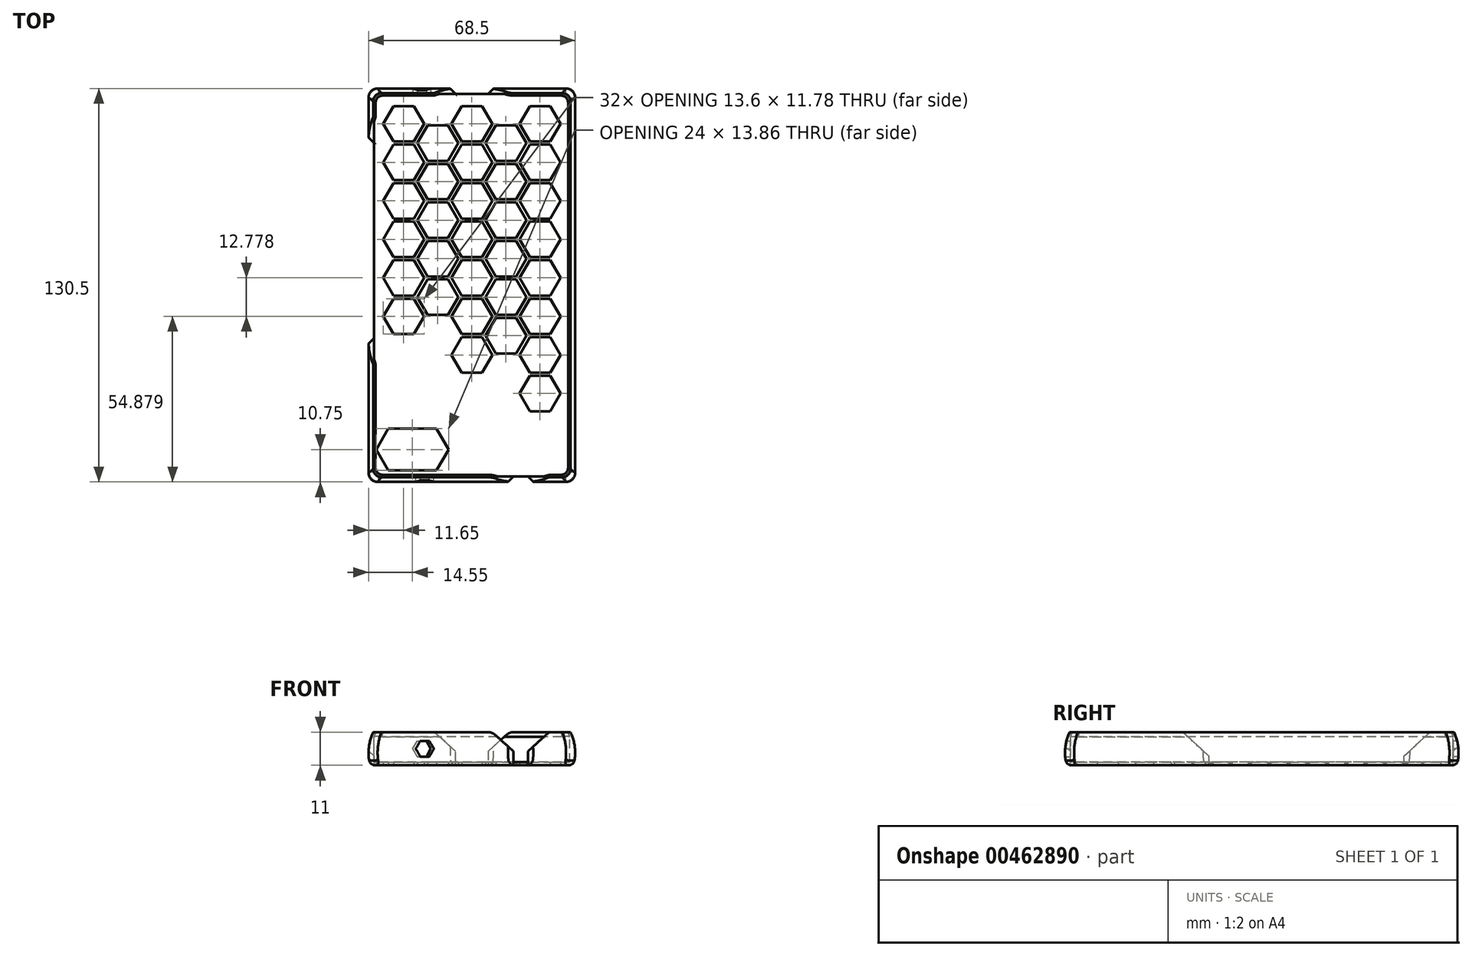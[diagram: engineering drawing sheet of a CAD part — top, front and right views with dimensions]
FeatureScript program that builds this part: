
annotation { "Feature Type Name" : "Feature", "Feature Type Description" : "" }
export const myFeature = defineFeature(function(context is Context, id is Id, definition is map)
    precondition{}
    {
        {
            var Q0;
            Q0=qCreatedBy(makeId("Top.planeOp"),FACE);
            var sketch = newSketch(context, id + "F0", { "sketchPlane" : qUnion([Q0])});
            skLineSegment(sketch, "E0.bottom", {"start": v(-32.9, 63.9) * mm, "end": v(32.9, 63.9) * mm});
            skLineSegment(sketch, "E0.top", {"start": v(-32.9, -63.9) * mm, "end": v(32.9, -63.9) * mm});
            skLineSegment(sketch, "E0.left", {"start": v(-32.9, 63.9) * mm, "end": v(-32.9, -63.9) * mm});
            skLineSegment(sketch, "E0.right", {"start": v(32.9, 63.9) * mm, "end": v(32.9, -63.9) * mm});
            skLineSegment(sketch, "E1", {"start": v(-32.9, 63.9) * mm, "end": v(32.9, -63.9) * mm, "construction": true});
            skLineSegment(sketch, "E2.bottom", {"start": v(-34.1, 65.1) * mm, "end": v(34.1, 65.1) * mm});
            skLineSegment(sketch, "E2.top", {"start": v(-34.1, -65.1) * mm, "end": v(34.1, -65.1) * mm});
            skLineSegment(sketch, "E2.left", {"start": v(-34.1, 65.1) * mm, "end": v(-34.1, -65.1) * mm});
            skLineSegment(sketch, "E2.right", {"start": v(34.1, 65.1) * mm, "end": v(34.1, -65.1) * mm});
            skLineSegment(sketch, "E3", {"start": v(34.1, 65.1) * mm, "end": v(-34.1, -65.1) * mm, "construction": true});
            skSolve(sketch);
        }
        {
            var Q0;
            Q0=makeQuery(id+"F0.imprint","IMPRINT",FACE,{"disambiguationData":[TD([[makeQuery(id+"F0.imprint","IMPRINT",EDGE,{"derivedFrom":sQuery(id+"F0.wireOp",EDGE,"E0.bottom")}),-1.0]])]});
            extrude(context, id + "F1", {"entities" : qUnion([Q0]), "depth" : 1 * mm});
        }
        {
            var Q0;
            Q0=makeQuery(id+"F1.opExtrude","SWEPT_FACE",FACE,{"disambiguationData":[OSD([sQuery(id+"F0.wireOp",EDGE,"E0.right")])]});
            var sketch = newSketch(context, id + "F2", { "sketchPlane" : qUnion([Q0])});
            skLineSegment(sketch, "E4", {"start": v(-63.9, 0) * mm, "end": v(-64.7, 0) * mm});
            skPoint(sketch, "E5.startSnap0", {"position": v(-64.3, 0) * mm});
            skLineSegment(sketch, "E6", {"start": v(-62.9, 11) * mm, "end": v(-63.7, 11) * mm});
            skArc(sketch, "E7", {"start": v(-63.7, 11) * mm, "mid": v(-65.18, 5.59) * mm, "end": v(-64.7, 0) * mm});
            skLineSegment(sketch, "E8", {"start": v(-63.9, 0) * mm, "end": v(-63.9, 1) * mm});
            skArc(sketch, "E9", {"start": v(-62.9, 11) * mm, "mid": v(-64.06, 6.07) * mm, "end": v(-63.9, 1) * mm});
            skLineSegment(sketch, "E10", {"start": v(-49.25, 4.14) * mm, "end": v(-44.8, 4.14) * mm, "construction": true});
            skLineSegment(sketch, "E11", {"start": v(-62.9, 11) * mm, "end": v(-62.9, 1) * mm, "construction": true});
            skLineSegment(sketch, "E12", {"start": v(-63.43, 1) * mm, "end": v(-63.43, 9.4) * mm});
            skSolve(sketch);
        }
        {
            var Q0;
            Q0=makeQuery(id+"F2.imprint","IMPRINT",FACE,{"disambiguationData":[TD([[makeQuery(id+"F2.imprint","IMPRINT",EDGE,{"derivedFrom":sQuery(id+"F2.wireOp",EDGE,"E4")}),-1.0]])]});
            var Q1;
            {var subQ3=sQuery(id+"F2.wireOp",EDGE,"E12");Q1=makeQuery(id+"F2.imprint","IMPRINT",FACE,{"disambiguationData":[TD([[makeQuery(id+"F2.imprint","IMPRINT",EDGE,{"derivedFrom":subQ3}),1.0]])]});}
            var Q2;
            Q2=makeQuery(id+"F1.opExtrude","CAP_EDGE",EDGE,{"disambiguationData":[OSD([sQuery(id+"F0.wireOp",EDGE,"E0.top")])],"isStart":false});
            var Q3;
            Q3=makeQuery(id+"F1.opExtrude","CAP_EDGE",EDGE,{"disambiguationData":[OSD([sQuery(id+"F0.wireOp",EDGE,"E0.left")])],"isStart":false});
            var Q4;
            Q4=makeQuery(id+"F1.opExtrude","CAP_EDGE",EDGE,{"disambiguationData":[OSD([sQuery(id+"F0.wireOp",EDGE,"E0.bottom")])],"isStart":false});
            var Q5;
            Q5=makeQuery(id+"F1.opExtrude","CAP_EDGE",EDGE,{"disambiguationData":[OSD([sQuery(id+"F0.wireOp",EDGE,"E0.right")])],"isStart":false});
            sweep(context, id + "F3", {"operationType" : NewBodyOperationType.ADD, "profiles" : qUnion([Q0, Q1]), "path" : qUnion([Q2, Q3, Q4, Q5])});
        }
        {
            var Q0;
            Q0=makeQuery(id+"F3.opSweep","MID_CAP_EDGE",EDGE,{"disambiguationData":[OSD([sQuery(id+"F0.wireOp",EDGE,"E0.bottom"),sQuery(id+"F0.wireOp",EDGE,"E0.right"),sQuery(id+"F2.wireOp",EDGE,"E7")])],"capPos":3.0});
            var Q1;
            Q1=makeQuery(id+"F3.opSweep","MID_CAP_EDGE",EDGE,{"disambiguationData":[OSD([sQuery(id+"F0.wireOp",EDGE,"E0.bottom"),sQuery(id+"F0.wireOp",EDGE,"E0.left"),sQuery(id+"F2.wireOp",EDGE,"E7")])],"capPos":2.0});
            var Q2;
            Q2=makeQuery(id+"F3.opSweep","MID_CAP_EDGE",EDGE,{"disambiguationData":[OSD([sQuery(id+"F0.wireOp",EDGE,"E0.top"),sQuery(id+"F0.wireOp",EDGE,"E0.left"),sQuery(id+"F2.wireOp",EDGE,"E7")])],"capPos":1.0});
            var Q3;
            Q3=makeQuery(id+"F3.opSweep","CAP_EDGE",EDGE,{"disambiguationData":[OSD([sQuery(id+"F0.wireOp",EDGE,"E0.top"),sQuery(id+"F0.wireOp",EDGE,"E0.right"),sQuery(id+"F2.wireOp",EDGE,"E7")])],"isStart":true});
            fillet(context, id + "F4", {"entities" : qUnion([Q0, Q1, Q2, Q3]), "radius" : 3 * mm, "tangentPropagation" : true, "allowEdgeOverflow" : false});
        }
        {
            var Q0;
            Q0=makeQuery(id+"F3.opSweep","MID_CAP_EDGE",EDGE,{"disambiguationData":[OSD([sQuery(id+"F0.wireOp",EDGE,"E0.bottom"),sQuery(id+"F0.wireOp",EDGE,"E0.right"),sQuery(id+"F2.wireOp",EDGE,"0y0pLbtj-wvh3-Di3X-naMg-oC3GUoqOavBz")])],"capPos":3.0});
            var Q1;
            Q1=makeQuery(id+"F3.opSweep","MID_CAP_EDGE",EDGE,{"disambiguationData":[OSD([sQuery(id+"F0.wireOp",EDGE,"E0.bottom"),sQuery(id+"F0.wireOp",EDGE,"E0.left"),sQuery(id+"F2.wireOp",EDGE,"0y0pLbtj-wvh3-Di3X-naMg-oC3GUoqOavBz")])],"capPos":2.0});
            var Q2;
            Q2=makeQuery(id+"F3.opSweep","CAP_EDGE",EDGE,{"disambiguationData":[OSD([sQuery(id+"F0.wireOp",EDGE,"E0.top"),sQuery(id+"F0.wireOp",EDGE,"E0.right"),sQuery(id+"F2.wireOp",EDGE,"0y0pLbtj-wvh3-Di3X-naMg-oC3GUoqOavBz")])],"isStart":true});
            var Q3;
            Q3=makeQuery(id+"F3.opSweep","MID_CAP_EDGE",EDGE,{"disambiguationData":[OSD([sQuery(id+"F0.wireOp",EDGE,"E0.top"),sQuery(id+"F0.wireOp",EDGE,"E0.left"),sQuery(id+"F2.wireOp",EDGE,"0y0pLbtj-wvh3-Di3X-naMg-oC3GUoqOavBz")])],"capPos":1.0});
            fillet(context, id + "F5", {"entities" : qUnion([Q0, Q1, Q2, Q3]), "radius" : 2.6 * mm, "tangentPropagation" : true, "allowEdgeOverflow" : false});
        }
        {
            var Q0;
            {var subQ0=sQuery(id+"F0.wireOp",EDGE,"E0.top");Q0=makeQuery(id+"F3.boolean.opBoolean","MERGE",FACE,{"derivedFrom":[makeQuery(id+"F1.opExtrude","CAP_FACE",FACE,{"disambiguationData":[OSD([sQuery(id+"F0.wireOp",EDGE,"E0.bottom"),subQ0,sQuery(id+"F0.wireOp",EDGE,"E0.left"),sQuery(id+"F0.wireOp",EDGE,"E0.right")])],"isStart":true}),makeQuery(id+"F3.opSweep","SWEPT_FACE",FACE,{"disambiguationData":[OSD([subQ0,sQuery(id+"F2.wireOp",EDGE,"E4")])]})]});}
            var sketch = newSketch(context, id + "F6", { "sketchPlane" : qUnion([Q0])});
            skLineSegment(sketch, "E13", {"start": v(0, -64.7) * mm, "end": v(0, 64.7) * mm, "construction": true});
            skLineSegment(sketch, "E14", {"start": v(-26, -34.85) * mm, "end": v(-29.4, -40.74) * mm});
            skLineSegment(sketch, "E15", {"start": v(-29.4, -40.74) * mm, "end": v(-26, -46.63) * mm});
            skLineSegment(sketch, "E16", {"start": v(-26, -46.63) * mm, "end": v(-19.2, -46.63) * mm});
            skLineSegment(sketch, "E17", {"start": v(-19.2, -46.63) * mm, "end": v(-15.8, -40.74) * mm});
            skLineSegment(sketch, "E18", {"start": v(-15.8, -40.74) * mm, "end": v(-19.2, -34.85) * mm});
            skLineSegment(sketch, "E19", {"start": v(-19.2, -34.85) * mm, "end": v(-26, -34.85) * mm});
            skLineSegment(sketch, "E20", {"start": v(-26, -34.85) * mm, "end": v(-26, -46.63) * mm, "construction": true});
            skLineSegment(sketch, "E21", {"start": v(-33.7, -40.74) * mm, "end": v(-29.4, -40.74) * mm, "construction": true});
            skLineSegment(sketch, "E22", {"start": v(-26, -46.63) * mm, "end": v(-19.2, -34.85) * mm, "construction": true});
            skLineSegment(sketch, "E23", {"start": v(-29.4, -40.74) * mm, "end": v(-15.8, -40.74) * mm, "construction": true});
            skLineSegment(sketch, "E24", {"start": v(-11.3, -64.7) * mm, "end": v(-11.3, 64.7) * mm, "construction": true});
            skLineSegment(sketch, "E25", {"start": v(-15.8, -40.74) * mm, "end": v(-11.3, -40.74) * mm, "construction": true});
            skLineSegment(sketch, "E26", {"start": v(-26, -34.85) * mm, "end": v(-19.2, -46.63) * mm, "construction": true});
            skLineSegment(sketch, "E27.MirrorCS", {"start": v(-6.8, -40.74) * mm, "end": v(-3.4, -34.85) * mm});
            skLineSegment(sketch, "E28.MirrorCS", {"start": v(-3.4, -34.85) * mm, "end": v(3.4, -34.85) * mm});
            skLineSegment(sketch, "E29.MirrorCS", {"start": v(3.4, -34.85) * mm, "end": v(6.8, -40.74) * mm});
            skLineSegment(sketch, "E30.MirrorCS", {"start": v(6.8, -40.74) * mm, "end": v(3.4, -46.63) * mm});
            skLineSegment(sketch, "E31.MirrorCS", {"start": v(3.4, -46.63) * mm, "end": v(-3.4, -46.63) * mm});
            skLineSegment(sketch, "E32.MirrorCS", {"start": v(-3.4, -46.63) * mm, "end": v(-6.8, -40.74) * mm});
            skPoint(sketch, "E33", {"position": v(0, -34.85) * mm});
            skLineSegment(sketch, "E34", {"start": v(11.3, -64.7) * mm, "end": v(11.3, 64.7) * mm, "construction": true});
            skLineSegment(sketch, "E35", {"start": v(6.8, -40.74) * mm, "end": v(11.3, -40.74) * mm, "construction": true});
            skLineSegment(sketch, "E36.MirrorCS", {"start": v(19.2, -34.85) * mm, "end": v(15.8, -40.74) * mm});
            skLineSegment(sketch, "E37.MirrorCS", {"start": v(26, -34.85) * mm, "end": v(19.2, -34.85) * mm});
            skLineSegment(sketch, "E38.MirrorCS", {"start": v(29.4, -40.74) * mm, "end": v(26, -34.85) * mm});
            skLineSegment(sketch, "E39.MirrorCS", {"start": v(26, -46.63) * mm, "end": v(29.4, -40.74) * mm});
            skLineSegment(sketch, "E40.MirrorCS", {"start": v(19.2, -46.63) * mm, "end": v(26, -46.63) * mm});
            skLineSegment(sketch, "E41.MirrorCS", {"start": v(15.8, -40.74) * mm, "end": v(19.2, -46.63) * mm});
            skLineSegment(sketch, "E42", {"start": v(-4.5, -34.35) * mm, "end": v(-7.9, -28.46) * mm});
            skLineSegment(sketch, "E43", {"start": v(-7.9, -28.46) * mm, "end": v(-14.7, -28.46) * mm});
            skLineSegment(sketch, "E44", {"start": v(-14.7, -28.46) * mm, "end": v(-18.1, -34.35) * mm});
            skLineSegment(sketch, "E45", {"start": v(-18.1, -34.35) * mm, "end": v(-4.5, -34.35) * mm, "construction": true});
            skLineSegment(sketch, "E46.MirrorCS", {"start": v(15.8, -40.74) * mm, "end": v(11.3, -40.74) * mm, "construction": true});
            skLineSegment(sketch, "E47", {"start": v(-18.1, -34.35) * mm, "end": v(-14.7, -40.24) * mm});
            skLineSegment(sketch, "E48", {"start": v(-14.7, -40.24) * mm, "end": v(-7.9, -40.24) * mm});
            skLineSegment(sketch, "E49", {"start": v(-7.9, -40.24) * mm, "end": v(-4.5, -34.35) * mm});
            skPoint(sketch, "E50", {"position": v(-11.3, -40.24) * mm});
            skLineSegment(sketch, "E51.MirrorCS", {"start": v(4.5, -34.35) * mm, "end": v(7.9, -28.46) * mm});
            skLineSegment(sketch, "E52.MirrorCS", {"start": v(7.9, -28.46) * mm, "end": v(14.7, -28.46) * mm});
            skLineSegment(sketch, "E53.MirrorCS", {"start": v(14.7, -28.46) * mm, "end": v(18.1, -34.35) * mm});
            skLineSegment(sketch, "E54.MirrorCS", {"start": v(18.1, -34.35) * mm, "end": v(14.7, -40.24) * mm});
            skLineSegment(sketch, "E55.MirrorCS", {"start": v(14.7, -40.24) * mm, "end": v(7.9, -40.24) * mm});
            skLineSegment(sketch, "E56.MirrorCS", {"start": v(7.9, -40.24) * mm, "end": v(4.5, -34.35) * mm});
            skLineSegment(sketch, "E57.MirrorCS", {"start": v(-19.2, -33.85) * mm, "end": v(-26, -33.85) * mm});
            skLineSegment(sketch, "E58.MirrorCS", {"start": v(-26, -33.85) * mm, "end": v(-29.4, -27.96) * mm});
            skLineSegment(sketch, "E59.MirrorCS", {"start": v(-29.4, -27.96) * mm, "end": v(-26, -22.07) * mm});
            skLineSegment(sketch, "E60.MirrorCS", {"start": v(-26, -22.07) * mm, "end": v(-19.2, -22.07) * mm});
            skLineSegment(sketch, "E61.MirrorCS", {"start": v(-19.2, -22.07) * mm, "end": v(-15.8, -27.96) * mm});
            skLineSegment(sketch, "E62.MirrorCS", {"start": v(-15.8, -27.96) * mm, "end": v(-19.2, -33.85) * mm});
            skLineSegment(sketch, "E63.MirrorCS", {"start": v(-6.8, -27.96) * mm, "end": v(-3.4, -33.85) * mm});
            skLineSegment(sketch, "E64.MirrorCS", {"start": v(-3.4, -33.85) * mm, "end": v(3.4, -33.85) * mm});
            skLineSegment(sketch, "E65.MirrorCS", {"start": v(3.4, -33.85) * mm, "end": v(6.8, -27.96) * mm});
            skLineSegment(sketch, "E66.MirrorCS", {"start": v(6.8, -27.96) * mm, "end": v(3.4, -22.07) * mm});
            skLineSegment(sketch, "E67.MirrorCS", {"start": v(3.4, -22.07) * mm, "end": v(-3.4, -22.07) * mm});
            skLineSegment(sketch, "E68.MirrorCS", {"start": v(-3.4, -22.07) * mm, "end": v(-6.8, -27.96) * mm});
            skLineSegment(sketch, "E69.MirrorCS", {"start": v(15.8, -27.96) * mm, "end": v(19.2, -22.07) * mm});
            skLineSegment(sketch, "E70.MirrorCS", {"start": v(19.2, -33.85) * mm, "end": v(15.8, -27.96) * mm});
            skLineSegment(sketch, "E71.MirrorCS", {"start": v(26, -33.85) * mm, "end": v(19.2, -33.85) * mm});
            skLineSegment(sketch, "E72.MirrorCS", {"start": v(29.4, -27.96) * mm, "end": v(26, -33.85) * mm});
            skLineSegment(sketch, "E73.MirrorCS", {"start": v(26, -22.07) * mm, "end": v(29.4, -27.96) * mm});
            skLineSegment(sketch, "E74.MirrorCS", {"start": v(19.2, -22.07) * mm, "end": v(26, -22.07) * mm});
            skLineSegment(sketch, "E75", {"start": v(-29.4, -27.96) * mm, "end": v(-15.8, -27.96) * mm, "construction": true});
            skLineSegment(sketch, "E76.MirrorCS", {"start": v(-7.9, -27.46) * mm, "end": v(-14.7, -27.46) * mm});
            skLineSegment(sketch, "E77.MirrorCS", {"start": v(-14.7, -27.46) * mm, "end": v(-18.1, -21.57) * mm});
            skLineSegment(sketch, "E78.MirrorCS", {"start": v(-18.1, -21.57) * mm, "end": v(-14.7, -15.69) * mm});
            skLineSegment(sketch, "E79.MirrorCS", {"start": v(-14.7, -15.69) * mm, "end": v(-7.9, -15.69) * mm});
            skLineSegment(sketch, "E80.MirrorCS", {"start": v(-7.9, -15.69) * mm, "end": v(-4.5, -21.57) * mm});
            skLineSegment(sketch, "E81.MirrorCS", {"start": v(-4.5, -21.57) * mm, "end": v(-7.9, -27.46) * mm});
            skLineSegment(sketch, "E82.MirrorCS", {"start": v(7.9, -15.69) * mm, "end": v(4.5, -21.57) * mm});
            skLineSegment(sketch, "E83.MirrorCS", {"start": v(4.5, -21.57) * mm, "end": v(7.9, -27.46) * mm});
            skLineSegment(sketch, "E84.MirrorCS", {"start": v(7.9, -27.46) * mm, "end": v(14.7, -27.46) * mm});
            skLineSegment(sketch, "E85.MirrorCS", {"start": v(14.7, -27.46) * mm, "end": v(18.1, -21.57) * mm});
            skLineSegment(sketch, "E86.MirrorCS", {"start": v(18.1, -21.57) * mm, "end": v(14.7, -15.69) * mm});
            skLineSegment(sketch, "E87.MirrorCS", {"start": v(14.7, -15.69) * mm, "end": v(7.9, -15.69) * mm});
            skLineSegment(sketch, "E88", {"start": v(-18.1, -21.57) * mm, "end": v(-4.5, -21.57) * mm, "construction": true});
            skLineSegment(sketch, "E89.MirrorCS", {"start": v(-19.2, -21.07) * mm, "end": v(-15.8, -15.19) * mm});
            skLineSegment(sketch, "E90.MirrorCS", {"start": v(-26, -21.07) * mm, "end": v(-19.2, -21.07) * mm});
            skLineSegment(sketch, "E91.MirrorCS", {"start": v(-29.4, -15.19) * mm, "end": v(-26, -21.07) * mm});
            skLineSegment(sketch, "E92.MirrorCS", {"start": v(-26, -9.3) * mm, "end": v(-29.4, -15.19) * mm});
            skLineSegment(sketch, "E93.MirrorCS", {"start": v(-19.2, -9.3) * mm, "end": v(-26, -9.3) * mm});
            skLineSegment(sketch, "E94.MirrorCS", {"start": v(-15.8, -15.19) * mm, "end": v(-19.2, -9.3) * mm});
            skLineSegment(sketch, "E95.MirrorCS", {"start": v(-29.4, -15.19) * mm, "end": v(-15.8, -15.19) * mm, "construction": true});
            skLineSegment(sketch, "E96.MirrorCS", {"start": v(-6.8, -15.19) * mm, "end": v(-3.4, -9.3) * mm});
            skLineSegment(sketch, "E97.MirrorCS", {"start": v(-3.4, -21.07) * mm, "end": v(-6.8, -15.19) * mm});
            skLineSegment(sketch, "E98.MirrorCS", {"start": v(3.4, -21.07) * mm, "end": v(-3.4, -21.07) * mm});
            skLineSegment(sketch, "E99.MirrorCS", {"start": v(6.8, -15.19) * mm, "end": v(3.4, -21.07) * mm});
            skLineSegment(sketch, "E100.MirrorCS", {"start": v(3.4, -9.3) * mm, "end": v(6.8, -15.19) * mm});
            skLineSegment(sketch, "E101.MirrorCS", {"start": v(-3.4, -9.3) * mm, "end": v(3.4, -9.3) * mm});
            skLineSegment(sketch, "E102.MirrorCS", {"start": v(19.2, -9.3) * mm, "end": v(15.8, -15.19) * mm});
            skLineSegment(sketch, "E103.MirrorCS", {"start": v(15.8, -15.19) * mm, "end": v(19.2, -21.07) * mm});
            skLineSegment(sketch, "E104.MirrorCS", {"start": v(19.2, -21.07) * mm, "end": v(26, -21.07) * mm});
            skLineSegment(sketch, "E105.MirrorCS", {"start": v(26, -21.07) * mm, "end": v(29.4, -15.19) * mm});
            skLineSegment(sketch, "E106.MirrorCS", {"start": v(29.4, -15.19) * mm, "end": v(26, -9.3) * mm});
            skLineSegment(sketch, "E107.MirrorCS", {"start": v(26, -9.3) * mm, "end": v(19.2, -9.3) * mm});
            skLineSegment(sketch, "E108.MirrorCS", {"start": v(-19.2, -9.3) * mm, "end": v(-15.8, -15.19) * mm});
            skLineSegment(sketch, "E109.MirrorCS", {"start": v(-26, -9.3) * mm, "end": v(-19.2, -9.3) * mm});
            skLineSegment(sketch, "E110.MirrorCS", {"start": v(-29.4, -15.19) * mm, "end": v(-26, -9.3) * mm});
            skLineSegment(sketch, "E111.MirrorCS", {"start": v(-26, -21.07) * mm, "end": v(-29.4, -15.19) * mm});
            skLineSegment(sketch, "E112.MirrorCS", {"start": v(-19.2, -21.07) * mm, "end": v(-26, -21.07) * mm});
            skLineSegment(sketch, "E113.MirrorCS", {"start": v(-15.8, -15.19) * mm, "end": v(-19.2, -21.07) * mm});
            skLineSegment(sketch, "E114.MirrorCS", {"start": v(-26, -8.3) * mm, "end": v(-19.2, -8.3) * mm});
            skLineSegment(sketch, "E115.MirrorCS", {"start": v(-29.4, -2.4) * mm, "end": v(-26, -8.3) * mm});
            skLineSegment(sketch, "E116.MirrorCS", {"start": v(-26, 3.48) * mm, "end": v(-29.4, -2.4) * mm});
            skLineSegment(sketch, "E117.MirrorCS", {"start": v(-19.2, 3.48) * mm, "end": v(-26, 3.48) * mm});
            skLineSegment(sketch, "E118.MirrorCS", {"start": v(-15.8, -2.4) * mm, "end": v(-19.2, 3.48) * mm});
            skLineSegment(sketch, "E119.MirrorCS", {"start": v(-19.2, -8.3) * mm, "end": v(-15.8, -2.4) * mm});
            skLineSegment(sketch, "E120.MirrorCS", {"start": v(-14.7, -2.9) * mm, "end": v(-18.1, -8.8) * mm});
            skLineSegment(sketch, "E121.MirrorCS", {"start": v(-18.1, -8.8) * mm, "end": v(-14.7, -14.69) * mm});
            skLineSegment(sketch, "E122.MirrorCS", {"start": v(-14.7, -14.69) * mm, "end": v(-7.9, -14.69) * mm});
            skLineSegment(sketch, "E123.MirrorCS", {"start": v(-7.9, -14.69) * mm, "end": v(-4.5, -8.8) * mm});
            skLineSegment(sketch, "E124.MirrorCS", {"start": v(-4.5, -8.8) * mm, "end": v(-7.9, -2.9) * mm});
            skLineSegment(sketch, "E125.MirrorCS", {"start": v(-7.9, -2.9) * mm, "end": v(-14.7, -2.9) * mm});
            skLineSegment(sketch, "E126.MirrorCS", {"start": v(3.4, -8.3) * mm, "end": v(-3.4, -8.3) * mm});
            skLineSegment(sketch, "E127.MirrorCS", {"start": v(-3.4, -8.3) * mm, "end": v(-6.8, -2.4) * mm});
            skLineSegment(sketch, "E128.MirrorCS", {"start": v(-6.8, -2.4) * mm, "end": v(-3.4, 3.48) * mm});
            skLineSegment(sketch, "E129.MirrorCS", {"start": v(-3.4, 3.48) * mm, "end": v(3.4, 3.48) * mm});
            skLineSegment(sketch, "E130.MirrorCS", {"start": v(3.4, 3.48) * mm, "end": v(6.8, -2.4) * mm});
            skLineSegment(sketch, "E131.MirrorCS", {"start": v(6.8, -2.4) * mm, "end": v(3.4, -8.3) * mm});
            skLineSegment(sketch, "E132.MirrorCS", {"start": v(14.7, -14.69) * mm, "end": v(7.9, -14.69) * mm});
            skLineSegment(sketch, "E133.MirrorCS", {"start": v(7.9, -14.69) * mm, "end": v(4.5, -8.8) * mm});
            skLineSegment(sketch, "E134.MirrorCS", {"start": v(4.5, -8.8) * mm, "end": v(7.9, -2.9) * mm});
            skLineSegment(sketch, "E135.MirrorCS", {"start": v(7.9, -2.9) * mm, "end": v(14.7, -2.9) * mm});
            skLineSegment(sketch, "E136.MirrorCS", {"start": v(14.7, -2.9) * mm, "end": v(18.1, -8.8) * mm});
            skLineSegment(sketch, "E137.MirrorCS", {"start": v(18.1, -8.8) * mm, "end": v(14.7, -14.69) * mm});
            skLineSegment(sketch, "E138.MirrorCS", {"start": v(15.8, -2.4) * mm, "end": v(19.2, -8.3) * mm});
            skLineSegment(sketch, "E139.MirrorCS", {"start": v(19.2, 3.48) * mm, "end": v(15.8, -2.4) * mm});
            skLineSegment(sketch, "E140.MirrorCS", {"start": v(26, 3.48) * mm, "end": v(19.2, 3.48) * mm});
            skLineSegment(sketch, "E141.MirrorCS", {"start": v(29.4, -2.4) * mm, "end": v(26, 3.48) * mm});
            skLineSegment(sketch, "E142.MirrorCS", {"start": v(26, -8.3) * mm, "end": v(29.4, -2.4) * mm});
            skLineSegment(sketch, "E143.MirrorCS", {"start": v(19.2, -8.3) * mm, "end": v(26, -8.3) * mm});
            skLineSegment(sketch, "E144", {"start": v(-11.7, 61.43) * mm, "end": v(-11.7, 47.57) * mm, "construction": true});
            skLineSegment(sketch, "E145", {"start": v(-29.4, -2.4) * mm, "end": v(-15.8, -2.4) * mm, "construction": true});
            skLineSegment(sketch, "E146.MirrorCS", {"start": v(-14.7, -1.9) * mm, "end": v(-18.1, 3.98) * mm});
            skLineSegment(sketch, "E147.MirrorCS", {"start": v(-7.9, -1.9) * mm, "end": v(-14.7, -1.9) * mm});
            skLineSegment(sketch, "E148.MirrorCS", {"start": v(-4.5, 3.98) * mm, "end": v(-7.9, -1.9) * mm});
            skLineSegment(sketch, "E149.MirrorCS", {"start": v(-7.9, 9.87) * mm, "end": v(-4.5, 3.98) * mm});
            skLineSegment(sketch, "E150.MirrorCS", {"start": v(-14.7, 9.87) * mm, "end": v(-7.9, 9.87) * mm});
            skLineSegment(sketch, "E151.MirrorCS", {"start": v(-18.1, 3.98) * mm, "end": v(-14.7, 9.87) * mm});
            skLineSegment(sketch, "E152.MirrorCS", {"start": v(4.5, 3.98) * mm, "end": v(7.9, -1.9) * mm});
            skLineSegment(sketch, "E153.MirrorCS", {"start": v(7.9, 9.87) * mm, "end": v(4.5, 3.98) * mm});
            skLineSegment(sketch, "E154.MirrorCS", {"start": v(14.7, 9.87) * mm, "end": v(7.9, 9.87) * mm});
            skLineSegment(sketch, "E155.MirrorCS", {"start": v(18.1, 3.98) * mm, "end": v(14.7, 9.87) * mm});
            skLineSegment(sketch, "E156.MirrorCS", {"start": v(14.7, -1.9) * mm, "end": v(18.1, 3.98) * mm});
            skLineSegment(sketch, "E157.MirrorCS", {"start": v(7.9, -1.9) * mm, "end": v(14.7, -1.9) * mm});
            skLineSegment(sketch, "E158.MirrorCS", {"start": v(26, 4.48) * mm, "end": v(19.2, 4.48) * mm});
            skLineSegment(sketch, "E159.MirrorCS", {"start": v(19.2, 4.48) * mm, "end": v(15.8, 10.37) * mm});
            skLineSegment(sketch, "E160.MirrorCS", {"start": v(15.8, 10.37) * mm, "end": v(19.2, 16.26) * mm});
            skLineSegment(sketch, "E161.MirrorCS", {"start": v(19.2, 16.26) * mm, "end": v(26, 16.26) * mm});
            skLineSegment(sketch, "E162.MirrorCS", {"start": v(26, 16.26) * mm, "end": v(29.4, 10.37) * mm});
            skLineSegment(sketch, "E163.MirrorCS", {"start": v(29.4, 10.37) * mm, "end": v(26, 4.48) * mm});
            skLineSegment(sketch, "E164.MirrorCS", {"start": v(14.7, 10.87) * mm, "end": v(7.9, 10.87) * mm});
            skLineSegment(sketch, "E165.MirrorCS", {"start": v(7.9, 10.87) * mm, "end": v(4.5, 16.76) * mm});
            skLineSegment(sketch, "E166.MirrorCS", {"start": v(4.5, 16.76) * mm, "end": v(7.9, 22.65) * mm});
            skLineSegment(sketch, "E167.MirrorCS", {"start": v(7.9, 22.65) * mm, "end": v(14.7, 22.65) * mm});
            skLineSegment(sketch, "E168.MirrorCS", {"start": v(14.7, 22.65) * mm, "end": v(18.1, 16.76) * mm});
            skLineSegment(sketch, "E169.MirrorCS", {"start": v(18.1, 16.76) * mm, "end": v(14.7, 10.87) * mm});
            skLineSegment(sketch, "E170.MirrorCS", {"start": v(6.8, 10.37) * mm, "end": v(3.4, 16.26) * mm});
            skLineSegment(sketch, "E171.MirrorCS", {"start": v(3.4, 16.26) * mm, "end": v(-3.4, 16.26) * mm});
            skLineSegment(sketch, "E172.MirrorCS", {"start": v(-3.4, 16.26) * mm, "end": v(-6.8, 10.37) * mm});
            skLineSegment(sketch, "E173.MirrorCS", {"start": v(-6.8, 10.37) * mm, "end": v(-3.4, 4.48) * mm});
            skLineSegment(sketch, "E174.MirrorCS", {"start": v(-3.4, 4.48) * mm, "end": v(3.4, 4.48) * mm});
            skLineSegment(sketch, "E175.MirrorCS", {"start": v(3.4, 4.48) * mm, "end": v(6.8, 10.37) * mm});
            skLineSegment(sketch, "E176.MirrorCS", {"start": v(15.8, 23.15) * mm, "end": v(19.2, 17.26) * mm});
            skLineSegment(sketch, "E177.MirrorCS", {"start": v(19.2, 29.04) * mm, "end": v(15.8, 23.15) * mm});
            skLineSegment(sketch, "E178.MirrorCS", {"start": v(26, 29.04) * mm, "end": v(19.2, 29.04) * mm});
            skLineSegment(sketch, "E179.MirrorCS", {"start": v(29.4, 23.15) * mm, "end": v(26, 29.04) * mm});
            skLineSegment(sketch, "E180.MirrorCS", {"start": v(26, 17.26) * mm, "end": v(29.4, 23.15) * mm});
            skLineSegment(sketch, "E181.MirrorCS", {"start": v(-19.2, 16.26) * mm, "end": v(-26, 16.26) * mm});
            skLineSegment(sketch, "E182.MirrorCS", {"start": v(-26, 16.26) * mm, "end": v(-29.4, 10.37) * mm});
            skLineSegment(sketch, "E183.MirrorCS", {"start": v(-29.4, 10.37) * mm, "end": v(-26, 4.48) * mm});
            skLineSegment(sketch, "E184.MirrorCS", {"start": v(-19.2, 4.48) * mm, "end": v(-26, 4.48) * mm});
            skLineSegment(sketch, "E185.MirrorCS", {"start": v(-15.8, 10.37) * mm, "end": v(-19.2, 4.48) * mm});
            skLineSegment(sketch, "E186.MirrorCS", {"start": v(-15.8, 10.37) * mm, "end": v(-19.2, 16.26) * mm});
            skLineSegment(sketch, "E187.MirrorCS", {"start": v(3.4, 17.26) * mm, "end": v(-3.4, 17.26) * mm});
            skLineSegment(sketch, "E188.MirrorCS", {"start": v(6.8, 23.15) * mm, "end": v(3.4, 17.26) * mm});
            skLineSegment(sketch, "E189.MirrorCS", {"start": v(3.4, 29.04) * mm, "end": v(6.8, 23.15) * mm});
            skLineSegment(sketch, "E190.MirrorCS", {"start": v(-3.4, 29.04) * mm, "end": v(3.4, 29.04) * mm});
            skLineSegment(sketch, "E191.MirrorCS", {"start": v(-6.8, 23.15) * mm, "end": v(-3.4, 29.04) * mm});
            skLineSegment(sketch, "E192.MirrorCS", {"start": v(-3.4, 17.26) * mm, "end": v(-6.8, 23.15) * mm});
            skLineSegment(sketch, "E193.MirrorCS", {"start": v(26, 30.04) * mm, "end": v(19.2, 30.04) * mm});
            skLineSegment(sketch, "E194.MirrorCS", {"start": v(19.2, 30.04) * mm, "end": v(15.8, 35.93) * mm});
            skLineSegment(sketch, "E195.MirrorCS", {"start": v(15.8, 35.93) * mm, "end": v(19.2, 41.82) * mm});
            skLineSegment(sketch, "E196.MirrorCS", {"start": v(19.2, 41.82) * mm, "end": v(26, 41.82) * mm});
            skLineSegment(sketch, "E197.MirrorCS", {"start": v(26, 41.82) * mm, "end": v(29.4, 35.93) * mm});
            skLineSegment(sketch, "E198.MirrorCS", {"start": v(29.4, 35.93) * mm, "end": v(26, 30.04) * mm});
            skLineSegment(sketch, "E199.MirrorCS", {"start": v(19.2, 17.26) * mm, "end": v(26, 17.26) * mm});
            skLineSegment(sketch, "E200", {"start": v(-27.7, 61.43) * mm, "end": v(-11.7, 61.43) * mm});
            skLineSegment(sketch, "E201", {"start": v(-27.7, 47.57) * mm, "end": v(-11.7, 47.57) * mm});
            skLineSegment(sketch, "E202", {"start": v(-27.7, 47.57) * mm, "end": v(-27.7, 61.43) * mm, "construction": true});
            skLineSegment(sketch, "E203", {"start": v(-27.7, 61.43) * mm, "end": v(-31.7, 54.5) * mm});
            skLineSegment(sketch, "E204", {"start": v(-31.7, 54.5) * mm, "end": v(-27.7, 47.57) * mm});
            skLineSegment(sketch, "E205", {"start": v(-11.7, 47.57) * mm, "end": v(-7.7, 54.5) * mm});
            skLineSegment(sketch, "E206", {"start": v(-7.7, 54.5) * mm, "end": v(-11.7, 61.43) * mm});
            skLineSegment(sketch, "E207", {"start": v(-33.7, 54.5) * mm, "end": v(-31.7, 54.5) * mm, "construction": true});
            skLineSegment(sketch, "E208.MirrorCS", {"start": v(18.1, -47.13) * mm, "end": v(14.7, -41.24) * mm});
            skLineSegment(sketch, "E209.MirrorCS", {"start": v(14.7, -41.24) * mm, "end": v(7.9, -41.24) * mm});
            skLineSegment(sketch, "E210.MirrorCS", {"start": v(7.9, -41.24) * mm, "end": v(4.5, -47.13) * mm});
            skLineSegment(sketch, "E211.MirrorCS", {"start": v(4.5, -47.13) * mm, "end": v(7.9, -53.02) * mm});
            skLineSegment(sketch, "E212.MirrorCS", {"start": v(7.9, -53.02) * mm, "end": v(14.7, -53.02) * mm});
            skLineSegment(sketch, "E213.MirrorCS", {"start": v(14.7, -53.02) * mm, "end": v(18.1, -47.13) * mm});
            skLineSegment(sketch, "E214.MirrorCS", {"start": v(-4.5, -47.13) * mm, "end": v(-7.9, -53.02) * mm});
            skLineSegment(sketch, "E215.MirrorCS", {"start": v(-7.9, -41.24) * mm, "end": v(-4.5, -47.13) * mm});
            skLineSegment(sketch, "E216.MirrorCS", {"start": v(-14.7, -41.24) * mm, "end": v(-7.9, -41.24) * mm});
            skLineSegment(sketch, "E217.MirrorCS", {"start": v(-18.1, -47.13) * mm, "end": v(-14.7, -41.24) * mm});
            skLineSegment(sketch, "E218.MirrorCS", {"start": v(-14.7, -53.02) * mm, "end": v(-18.1, -47.13) * mm});
            skLineSegment(sketch, "E219.MirrorCS", {"start": v(-7.9, -53.02) * mm, "end": v(-14.7, -53.02) * mm});
            skLineSegment(sketch, "E220.MirrorCS", {"start": v(-15.8, -53.52) * mm, "end": v(-19.2, -47.63) * mm});
            skLineSegment(sketch, "E221.MirrorCS", {"start": v(-19.2, -47.63) * mm, "end": v(-26, -47.63) * mm});
            skLineSegment(sketch, "E222.MirrorCS", {"start": v(-26, -47.63) * mm, "end": v(-29.4, -53.52) * mm});
            skLineSegment(sketch, "E223.MirrorCS", {"start": v(-29.4, -53.52) * mm, "end": v(-26, -59.4) * mm});
            skLineSegment(sketch, "E224.MirrorCS", {"start": v(-26, -59.4) * mm, "end": v(-19.2, -59.4) * mm});
            skLineSegment(sketch, "E225.MirrorCS", {"start": v(-19.2, -59.4) * mm, "end": v(-15.8, -53.52) * mm});
            skLineSegment(sketch, "E226.MirrorCS", {"start": v(-6.8, -53.52) * mm, "end": v(-3.4, -47.63) * mm});
            skLineSegment(sketch, "E227.MirrorCS", {"start": v(-3.4, -59.4) * mm, "end": v(-6.8, -53.52) * mm});
            skLineSegment(sketch, "E228.MirrorCS", {"start": v(3.4, -59.4) * mm, "end": v(-3.4, -59.4) * mm});
            skLineSegment(sketch, "E229.MirrorCS", {"start": v(6.8, -53.52) * mm, "end": v(3.4, -59.4) * mm});
            skLineSegment(sketch, "E230.MirrorCS", {"start": v(3.4, -47.63) * mm, "end": v(6.8, -53.52) * mm});
            skLineSegment(sketch, "E231.MirrorCS", {"start": v(-3.4, -47.63) * mm, "end": v(3.4, -47.63) * mm});
            skLineSegment(sketch, "E232.MirrorCS", {"start": v(19.2, -47.63) * mm, "end": v(15.8, -53.52) * mm});
            skLineSegment(sketch, "E233.MirrorCS", {"start": v(15.8, -53.52) * mm, "end": v(19.2, -59.4) * mm});
            skLineSegment(sketch, "E234.MirrorCS", {"start": v(19.2, -59.4) * mm, "end": v(26, -59.4) * mm});
            skLineSegment(sketch, "E235.MirrorCS", {"start": v(26, -59.4) * mm, "end": v(29.4, -53.52) * mm});
            skLineSegment(sketch, "E236.MirrorCS", {"start": v(29.4, -53.52) * mm, "end": v(26, -47.63) * mm});
            skLineSegment(sketch, "E237.MirrorCS", {"start": v(26, -47.63) * mm, "end": v(19.2, -47.63) * mm});
            skLineSegment(sketch, "E238", {"start": v(-29.4, -40.74) * mm, "end": v(-30.8, -64.7) * mm, "construction": true});
            skLineSegment(sketch, "E239", {"start": v(29.4, -40.74) * mm, "end": v(33.7, -40.74) * mm, "construction": true});
            skLineSegment(sketch, "E240", {"start": v(-27.7, 61.43) * mm, "end": v(-27.7, 63.43) * mm, "construction": true});
            skSolve(sketch);
        }
        {
            var Q0;
            Q0 = qSketchRegion(id + "F6", true);
            var Q1;
            Q1=makeQuery(id+"F1.opExtrude","CAP_FACE",FACE,{"disambiguationData":[OSD([sQuery(id+"F0.wireOp",EDGE,"E0.bottom"),sQuery(id+"F0.wireOp",EDGE,"E0.top"),sQuery(id+"F0.wireOp",EDGE,"E0.left"),sQuery(id+"F0.wireOp",EDGE,"E0.right")])],"isStart":false});
            extrude(context, id + "F7", {"entities" : qUnion([Q0]), "operationType" : NewBodyOperationType.REMOVE, "endBound" : BoundingType.UP_TO_SURFACE, "oppositeDirection" : true, "endBoundEntityFace" : qUnion([Q1]), "depth" : 25 * mm});
        }
        {
            var Q0;
            Q0=qCreatedBy(makeId("Right.planeOp"),FACE);
            var sketch = newSketch(context, id + "F8", { "sketchPlane" : qUnion([Q0])});
            skLineSegment(sketch, "E241", {"start": v(49.8, 5.5) * mm, "end": v(49.8, 1) * mm});
            skLineSegment(sketch, "E242", {"start": v(49.8, 1) * mm, "end": v(-20.2, 1) * mm});
            skLineSegment(sketch, "E243", {"start": v(-20.2, 1) * mm, "end": v(-20.2, 5.5) * mm});
            skLineSegment(sketch, "E244", {"start": v(-20.2, 5.5) * mm, "end": v(-26.2, 11) * mm});
            skLineSegment(sketch, "E245", {"start": v(60.99, 11) * mm, "end": v(-26.2, 11) * mm});
            skLineSegment(sketch, "E246", {"start": v(55.8, 11) * mm, "end": v(55.8, 0) * mm, "construction": true});
            skLineSegment(sketch, "E247", {"start": v(55.8, 11) * mm, "end": v(49.8, 5.5) * mm});
            skLineSegment(sketch, "E248", {"start": v(55.8, 5.5) * mm, "end": v(49.8, 5.5) * mm, "construction": true});
            skSolve(sketch);
        }
        {
            var Q0;
            Q0 = qSketchRegion(id + "F8", true);
            extrude(context, id + "F9", {"entities" : qUnion([Q0]), "operationType" : NewBodyOperationType.REMOVE, "oppositeDirection" : true, "depth" : 50 * mm});
        }
        {
            var Q0;
            Q0=qCreatedBy(makeId("Front.planeOp"),FACE);
            var sketch = newSketch(context, id + "F10", { "sketchPlane" : qUnion([Q0])});
            skLineSegment(sketch, "E249", {"start": v(12.47, 11) * mm, "end": v(8, 7) * mm});
            skLineSegment(sketch, "E250", {"start": v(8, 7) * mm, "end": v(8, 1) * mm});
            skLineSegment(sketch, "E251", {"start": v(8, 1) * mm, "end": v(-8, 1) * mm});
            skLineSegment(sketch, "E252", {"start": v(-8, 1) * mm, "end": v(-8, 7) * mm});
            skLineSegment(sketch, "E253", {"start": v(-8, 7) * mm, "end": v(-12.47, 11) * mm});
            skPoint(sketch, "E254", {"position": v(0, 1) * mm});
            skLineSegment(sketch, "E255", {"start": v(12.47, 11) * mm, "end": v(-12.47, 11) * mm});
            skLineSegment(sketch, "E256", {"start": v(-15.1, 8.1) * mm, "end": v(-13.6, 5.5) * mm});
            skLineSegment(sketch, "E257", {"start": v(-13.6, 5.5) * mm, "end": v(-15.1, 2.9) * mm});
            skLineSegment(sketch, "E258", {"start": v(-15.1, 2.9) * mm, "end": v(-18.1, 2.9) * mm});
            skLineSegment(sketch, "E259", {"start": v(-18.1, 2.9) * mm, "end": v(-19.6, 5.5) * mm});
            skLineSegment(sketch, "E260", {"start": v(-19.6, 5.5) * mm, "end": v(-18.1, 8.1) * mm});
            skLineSegment(sketch, "E261", {"start": v(-18.1, 8.1) * mm, "end": v(-15.1, 8.1) * mm});
            skLineSegment(sketch, "E262", {"start": v(-15.1, 8.1) * mm, "end": v(-15.1, 2.9) * mm, "construction": true});
            skLineSegment(sketch, "E263", {"start": v(-13.6, 5.5) * mm, "end": v(-18.1, 2.9) * mm, "construction": true});
            skLineSegment(sketch, "E264", {"start": v(-15.1, 8.1) * mm, "end": v(-15.1, 11) * mm, "construction": true});
            skLineSegment(sketch, "E265", {"start": v(-15.1, 2.9) * mm, "end": v(-15.1, 0) * mm, "construction": true});
            skSolve(sketch);
        }
        {
            var Q0;
            Q0 = qSketchRegion(id + "F10", true);
            extrude(context, id + "F11", {"entities" : qUnion([Q0]), "operationType" : NewBodyOperationType.REMOVE, "oppositeDirection" : true, "depth" : 100 * mm, "offsetDistance" : 25 * mm});
        }
        {
            var Q0;
            Q0=qCreatedBy(makeId("Front.planeOp"),FACE);
            var sketch = newSketch(context, id + "F12", { "sketchPlane" : qUnion([Q0])});
            skLineSegment(sketch, "E266", {"start": v(6.7, 11) * mm, "end": v(11.17, 7) * mm});
            skLineSegment(sketch, "E267", {"start": v(11.17, 7) * mm, "end": v(11.17, 1) * mm});
            skLineSegment(sketch, "E268", {"start": v(11.17, 1) * mm, "end": v(21.17, 1) * mm});
            skLineSegment(sketch, "E269", {"start": v(21.17, 1) * mm, "end": v(21.17, 7) * mm});
            skLineSegment(sketch, "E270", {"start": v(21.17, 7) * mm, "end": v(25.65, 11) * mm});
            skLineSegment(sketch, "E271", {"start": v(6.7, 11) * mm, "end": v(25.65, 11) * mm});
            skSolve(sketch);
        }
        {
            var Q0;
            Q0=makeQuery(id+"F12.imprint","IMPRINT",FACE,{"disambiguationData":[TD([[makeQuery(id+"F12.imprint","IMPRINT",EDGE,{"derivedFrom":sQuery(id+"F12.wireOp",EDGE,"E266")}),1.0]])]});
            extrude(context, id + "F13", {"entities" : qUnion([Q0]), "operationType" : NewBodyOperationType.REMOVE, "depth" : 200 * mm, "offsetDistance" : 25 * mm});
        }
        {
            var Q0;
            Q0=qCreatedBy(makeId("Front.planeOp"),FACE);
            var sketch = newSketch(context, id + "F14", { "sketchPlane" : qUnion([Q0])});
            skLineSegment(sketch, "E272", {"start": v(-17.1, 8.1) * mm, "end": v(-18.6, 5.5) * mm});
            skLineSegment(sketch, "E273", {"start": v(-18.6, 5.5) * mm, "end": v(-17.1, 2.9) * mm});
            skLineSegment(sketch, "E274", {"start": v(-17.1, 2.9) * mm, "end": v(-14.1, 2.9) * mm});
            skLineSegment(sketch, "E275", {"start": v(-14.1, 2.9) * mm, "end": v(-12.6, 5.5) * mm});
            skLineSegment(sketch, "E276", {"start": v(-12.6, 5.5) * mm, "end": v(-14.1, 8.1) * mm});
            skLineSegment(sketch, "E277", {"start": v(-14.1, 8.1) * mm, "end": v(-17.1, 8.1) * mm});
            skLineSegment(sketch, "E278", {"start": v(-17.1, 8.1) * mm, "end": v(-17.1, 2.9) * mm, "construction": true});
            skLineSegment(sketch, "E279", {"start": v(-17.1, 8.1) * mm, "end": v(-14.1, 2.9) * mm, "construction": true});
            skLineSegment(sketch, "E280", {"start": v(-12.6, 5.5) * mm, "end": v(-18.6, 5.5) * mm, "construction": true});
            skLineSegment(sketch, "E281", {"start": v(-17.1, 2.9) * mm, "end": v(-14.1, 8.1) * mm, "construction": true});
            skLineSegment(sketch, "E282", {"start": v(-14.1, 2.9) * mm, "end": v(-14.1, 0) * mm, "construction": true});
            skLineSegment(sketch, "E283", {"start": v(-14.1, 8.1) * mm, "end": v(-14.1, 11) * mm, "construction": true});
            skSolve(sketch);
        }
        {
            var Q0;
            {var subQ2=sQuery(id+"F0.wireOp",EDGE,"E0.right");var subQ3=sQuery(id+"F0.wireOp",EDGE,"E0.left");var subQ4=sQuery(id+"F0.wireOp",EDGE,"E0.top");var subQ5=sQuery(id+"F0.wireOp",EDGE,"E0.bottom");var subQ6=makeQuery(id+"F1.opExtrude","CAP_FACE",FACE,{"disambiguationData":[OSD([subQ5,subQ4,subQ3,subQ2])],"isStart":false});Q0=makeQuery(id+"F13.boolean.opBoolean","MERGE",FACE,{"derivedFrom":[makeQuery(id+"F11.boolean.opBoolean","MERGE",FACE,{"derivedFrom":[makeQuery(id+"F9.boolean.opBoolean","MERGE",FACE,{"derivedFrom":[makeQuery(id+"F7.boolean.opBoolean","SPLIT",FACE,{"disambiguationData":[TD([makeQuery(id+"F7.opExtrude","SWEPT_FACE",FACE,{"disambiguationData":[OSD([sQuery(id+"F6.wireOp",EDGE,"E14")])]})])],"derivedFrom":subQ6}),makeQuery(id+"F9.opExtrude","SWEPT_FACE",FACE,{"disambiguationData":[OSD([sQuery(id+"F8.wireOp",EDGE,"E242")])]})]}),makeQuery(id+"F11.opExtrude","SWEPT_FACE",FACE,{"disambiguationData":[OSD([sQuery(id+"F10.wireOp",EDGE,"E251")])]})]}),makeQuery(id+"F13.opExtrude","SWEPT_FACE",FACE,{"disambiguationData":[OSD([sQuery(id+"F12.wireOp",EDGE,"E268")])]})]});}
            var sketch = newSketch(context, id + "F15", { "sketchPlane" : qUnion([Q0])});
            skLineSegment(sketch, "E284", {"start": v(-33.93, 49.8) * mm, "end": v(-32.43, 49.8) * mm});
            skLineSegment(sketch, "E285", {"start": v(-32.43, 49.8) * mm, "end": v(-32.43, -20.2) * mm});
            skLineSegment(sketch, "E286", {"start": v(-32.43, -20.2) * mm, "end": v(-33.93, -20.2) * mm});
            skLineSegment(sketch, "E287", {"start": v(-33.93, -20.2) * mm, "end": v(-33.93, 49.8) * mm});
            skLineSegment(sketch, "E288", {"start": v(-8, 63.43) * mm, "end": v(8, 63.43) * mm});
            skLineSegment(sketch, "E289", {"start": v(8, 63.43) * mm, "end": v(8, 64.93) * mm});
            skLineSegment(sketch, "E290", {"start": v(8, 64.93) * mm, "end": v(-8, 64.93) * mm});
            skLineSegment(sketch, "E291", {"start": v(-8, 64.93) * mm, "end": v(-8, 63.43) * mm});
            skLineSegment(sketch, "E292", {"start": v(11.17, -63.43) * mm, "end": v(21.17, -63.43) * mm});
            skLineSegment(sketch, "E293", {"start": v(21.17, -63.43) * mm, "end": v(21.17, -64.93) * mm});
            skLineSegment(sketch, "E294", {"start": v(21.17, -64.93) * mm, "end": v(11.17, -64.93) * mm});
            skLineSegment(sketch, "E295", {"start": v(11.17, -64.93) * mm, "end": v(11.17, -63.43) * mm});
            skSolve(sketch);
        }
        {
            var Q0;
            Q0 = qSketchRegion(id + "F15", true);
            extrude(context, id + "F16", {"entities" : qUnion([Q0]), "operationType" : NewBodyOperationType.REMOVE, "oppositeDirection" : true, "depth" : 25 * mm, "offsetDistance" : 25 * mm});
        }
        {
            var Q0;
            Q0=makeQuery(id+"F16.boolean.opBoolean","COPY",EDGE,{"derivedFrom":makeQuery(id+"F16.opExtrude","SWEPT_EDGE",EDGE,{"disambiguationData":[OSD([sQuery(id+"F0.wireOp",EDGE,"E0.bottom"),sQuery(id+"F0.wireOp",EDGE,"E0.top"),sQuery(id+"F0.wireOp",EDGE,"E0.left"),sQuery(id+"F0.wireOp",EDGE,"E0.right"),sQuery(id+"F2.wireOp",EDGE,"0y0pLbtj-wvh3-Di3X-naMg-oC3GUoqOavBz"),sQuery(id+"F2.wireOp",EDGE,"E8"),sQuery(id+"F15.wireOp",EDGE,"E285"),sQuery(id+"F15.wireOp",EDGE,"E286")])]})});
            var Q1;
            Q1=makeQuery(id+"F16.boolean.opBoolean","COPY",EDGE,{"derivedFrom":makeQuery(id+"F16.opExtrude","SWEPT_EDGE",EDGE,{"disambiguationData":[OSD([sQuery(id+"F0.wireOp",EDGE,"E0.bottom"),sQuery(id+"F0.wireOp",EDGE,"E0.top"),sQuery(id+"F0.wireOp",EDGE,"E0.left"),sQuery(id+"F0.wireOp",EDGE,"E0.right"),sQuery(id+"F2.wireOp",EDGE,"0y0pLbtj-wvh3-Di3X-naMg-oC3GUoqOavBz"),sQuery(id+"F2.wireOp",EDGE,"E8"),sQuery(id+"F15.wireOp",EDGE,"E284"),sQuery(id+"F15.wireOp",EDGE,"E285")])]})});
            var Q2;
            Q2=makeQuery(id+"F16.boolean.opBoolean","COPY",EDGE,{"derivedFrom":makeQuery(id+"F16.opExtrude","SWEPT_EDGE",EDGE,{"disambiguationData":[OSD([sQuery(id+"F0.wireOp",EDGE,"E0.bottom"),sQuery(id+"F0.wireOp",EDGE,"E0.top"),sQuery(id+"F0.wireOp",EDGE,"E0.left"),sQuery(id+"F0.wireOp",EDGE,"E0.right"),sQuery(id+"F2.wireOp",EDGE,"0y0pLbtj-wvh3-Di3X-naMg-oC3GUoqOavBz"),sQuery(id+"F2.wireOp",EDGE,"E8"),sQuery(id+"F15.wireOp",EDGE,"E288"),sQuery(id+"F15.wireOp",EDGE,"E289")])]})});
            var Q3;
            Q3=makeQuery(id+"F16.boolean.opBoolean","COPY",EDGE,{"derivedFrom":makeQuery(id+"F16.opExtrude","SWEPT_EDGE",EDGE,{"disambiguationData":[OSD([sQuery(id+"F0.wireOp",EDGE,"E0.bottom"),sQuery(id+"F0.wireOp",EDGE,"E0.top"),sQuery(id+"F0.wireOp",EDGE,"E0.left"),sQuery(id+"F0.wireOp",EDGE,"E0.right"),sQuery(id+"F2.wireOp",EDGE,"0y0pLbtj-wvh3-Di3X-naMg-oC3GUoqOavBz"),sQuery(id+"F2.wireOp",EDGE,"E8"),sQuery(id+"F15.wireOp",EDGE,"E288"),sQuery(id+"F15.wireOp",EDGE,"E291")])]})});
            var Q4;
            Q4=makeQuery(id+"F16.boolean.opBoolean","COPY",EDGE,{"derivedFrom":makeQuery(id+"F16.opExtrude","SWEPT_EDGE",EDGE,{"disambiguationData":[OSD([sQuery(id+"F0.wireOp",EDGE,"E0.bottom"),sQuery(id+"F0.wireOp",EDGE,"E0.top"),sQuery(id+"F0.wireOp",EDGE,"E0.left"),sQuery(id+"F0.wireOp",EDGE,"E0.right"),sQuery(id+"F2.wireOp",EDGE,"0y0pLbtj-wvh3-Di3X-naMg-oC3GUoqOavBz"),sQuery(id+"F2.wireOp",EDGE,"E8"),sQuery(id+"F15.wireOp",EDGE,"E292"),sQuery(id+"F15.wireOp",EDGE,"E293")])]})});
            var Q5;
            Q5=makeQuery(id+"F16.boolean.opBoolean","COPY",EDGE,{"derivedFrom":makeQuery(id+"F16.opExtrude","SWEPT_EDGE",EDGE,{"disambiguationData":[OSD([sQuery(id+"F0.wireOp",EDGE,"E0.bottom"),sQuery(id+"F0.wireOp",EDGE,"E0.top"),sQuery(id+"F0.wireOp",EDGE,"E0.left"),sQuery(id+"F0.wireOp",EDGE,"E0.right"),sQuery(id+"F2.wireOp",EDGE,"0y0pLbtj-wvh3-Di3X-naMg-oC3GUoqOavBz"),sQuery(id+"F2.wireOp",EDGE,"E8"),sQuery(id+"F15.wireOp",EDGE,"E292"),sQuery(id+"F15.wireOp",EDGE,"E295")])]})});
            chamfer(context, id + "F17", {"entities" : qUnion([Q0, Q1, Q2, Q3, Q4, Q5]), "width" : 2.6 * mm, "tangentPropagation" : true});
        }
        {
            var Q0;
            {var subQ0=sQuery(id+"F2.wireOp",EDGE,"E7");var subQ1=sQuery(id+"F0.wireOp",EDGE,"E0.left");var subQ3=sQuery(id+"F2.wireOp",EDGE,"E4");Q0=makeQuery(id+"F16.boolean.opBoolean","SPLIT",EDGE,{"disambiguationData":[TD([makeQuery(id+"F9.boolean.opBoolean","COPY",FACE,{"derivedFrom":makeQuery(id+"F9.opExtrude","SWEPT_FACE",FACE,{"disambiguationData":[OSD([sQuery(id+"F8.wireOp",EDGE,"E243")])]})})])],"derivedFrom":makeQuery(id+"F3.opSweep","SWEPT_EDGE",EDGE,{"disambiguationData":[OSD([subQ1,subQ3,subQ0])]})});}
            var Q1;
            {var subQ0=sQuery(id+"F2.wireOp",EDGE,"E7");var subQ2=sQuery(id+"F0.wireOp",EDGE,"E0.top");var subQ3=sQuery(id+"F2.wireOp",EDGE,"E4");Q1=makeQuery(id+"F16.boolean.opBoolean","SPLIT",EDGE,{"disambiguationData":[TD([makeQuery(id+"F13.boolean.opBoolean","COPY",FACE,{"derivedFrom":makeQuery(id+"F13.opExtrude","SWEPT_FACE",FACE,{"disambiguationData":[OSD([sQuery(id+"F12.wireOp",EDGE,"E269")])]})})])],"derivedFrom":makeQuery(id+"F3.opSweep","SWEPT_EDGE",EDGE,{"disambiguationData":[OSD([subQ2,subQ3,subQ0])]})});}
            var Q2;
            {var subQ0=sQuery(id+"F2.wireOp",EDGE,"E7");var subQ2=sQuery(id+"F0.wireOp",EDGE,"E0.bottom");var subQ4=sQuery(id+"F2.wireOp",EDGE,"E4");Q2=makeQuery(id+"F16.boolean.opBoolean","SPLIT",EDGE,{"disambiguationData":[TD([makeQuery(id+"F11.boolean.opBoolean","COPY",FACE,{"derivedFrom":makeQuery(id+"F11.opExtrude","SWEPT_FACE",FACE,{"disambiguationData":[OSD([sQuery(id+"F10.wireOp",EDGE,"E252")])]})})])],"derivedFrom":makeQuery(id+"F3.opSweep","SWEPT_EDGE",EDGE,{"disambiguationData":[OSD([subQ2,subQ4,subQ0])]})});}
            fillet(context, id + "F18", {"entities" : qUnion([Q0, Q1, Q2]), "radius" : 2 * mm, "tangentPropagation" : true, "allowEdgeOverflow" : false});
        }
        {
            var Q0;
            Q0=makeQuery(id+"F9.boolean.opBoolean","COPY",EDGE,{"derivedFrom":makeQuery(id+"F9.opExtrude","SWEPT_EDGE",EDGE,{"disambiguationData":[OSD([sQuery(id+"F8.wireOp",EDGE,"E244"),sQuery(id+"F8.wireOp",EDGE,"E245")])]})});
            var Q1;
            Q1=makeQuery(id+"F13.boolean.opBoolean","COPY",EDGE,{"derivedFrom":makeQuery(id+"F13.opExtrude","SWEPT_EDGE",EDGE,{"disambiguationData":[OSD([sQuery(id+"F12.wireOp",EDGE,"E266"),sQuery(id+"F12.wireOp",EDGE,"E271")])]})});
            var Q2;
            Q2=makeQuery(id+"F13.boolean.opBoolean","COPY",EDGE,{"derivedFrom":makeQuery(id+"F13.opExtrude","SWEPT_EDGE",EDGE,{"disambiguationData":[OSD([sQuery(id+"F12.wireOp",EDGE,"E270"),sQuery(id+"F12.wireOp",EDGE,"E271")])]})});
            var Q3;
            Q3=makeQuery(id+"F11.boolean.opBoolean","COPY",EDGE,{"derivedFrom":makeQuery(id+"F11.opExtrude","SWEPT_EDGE",EDGE,{"disambiguationData":[OSD([sQuery(id+"F10.wireOp",EDGE,"E249"),sQuery(id+"F10.wireOp",EDGE,"E255")])]})});
            var Q4;
            Q4=makeQuery(id+"F11.boolean.opBoolean","COPY",EDGE,{"derivedFrom":makeQuery(id+"F11.opExtrude","SWEPT_EDGE",EDGE,{"disambiguationData":[OSD([sQuery(id+"F10.wireOp",EDGE,"E253"),sQuery(id+"F10.wireOp",EDGE,"E255")])]})});
            var Q5;
            Q5=makeQuery(id+"F9.boolean.opBoolean","COPY",EDGE,{"derivedFrom":makeQuery(id+"F9.opExtrude","SWEPT_EDGE",EDGE,{"disambiguationData":[OSD([sQuery(id+"F8.wireOp",EDGE,"E245"),sQuery(id+"F8.wireOp",EDGE,"E247")])]})});
            chamfer(context, id + "F19", {"entities" : qUnion([Q0, Q1, Q2, Q3, Q4, Q5]), "width" : 2 * mm, "tangentPropagation" : true});
        }
        {
            var Q0;
            Q0 = qSketchRegion(id + "F14", true);
            extrude(context, id + "F20", {"entities" : qUnion([Q0]), "operationType" : NewBodyOperationType.REMOVE, "depth" : 100 * mm, "offsetDistance" : 25 * mm});
        }
        {
            var Q0;
            {var subQ0=sQuery(id+"F2.wireOp",EDGE,"E12");var subQ1=sQuery(id+"F0.wireOp",EDGE,"E0.bottom");var subQ3=sQuery(id+"F0.wireOp",EDGE,"E0.right");Q0=makeQuery(id+"F11.boolean.opBoolean","SPLIT",EDGE,{"disambiguationData":[TD([makeQuery(id+"F11.opExtrude","SWEPT_FACE",FACE,{"disambiguationData":[OSD([sQuery(id+"F10.wireOp",EDGE,"E252")])]})])],"derivedFrom":makeQuery(id+"F3.opSweep","SWEPT_EDGE",EDGE,{"disambiguationData":[OSD([subQ1,subQ3,subQ0])]})});}
            var Q1;
            {var subQ0=sQuery(id+"F0.wireOp",EDGE,"E0.left");var subQ1=sQuery(id+"F0.wireOp",EDGE,"E0.bottom");Q1=makeQuery(id+"F5.opFillet","BLEND_EDGE",EDGE,{"blendedFrom":[makeQuery(id+"F3.opSweep","MID_CAP_EDGE",EDGE,{"disambiguationData":[OSD([subQ1,subQ0,sQuery(id+"F2.wireOp",EDGE,"E12")])],"capPos":2.0}),makeQuery(id+"F1.opExtrude","CAP_FACE",FACE,{"disambiguationData":[OSD([subQ1,sQuery(id+"F0.wireOp",EDGE,"E0.top"),subQ0,sQuery(id+"F0.wireOp",EDGE,"E0.right")])],"isStart":false})],"blendedInto":[makeQuery(id+"F1.opExtrude","CAP_FACE",FACE,{"disambiguationData":[OSD([subQ1,sQuery(id+"F0.wireOp",EDGE,"E0.top"),subQ0,sQuery(id+"F0.wireOp",EDGE,"E0.right")])],"isStart":false})]});}
            var Q2;
            {var subQ0=sQuery(id+"F2.wireOp",EDGE,"E12");var subQ1=sQuery(id+"F0.wireOp",EDGE,"E0.right");var subQ2=sQuery(id+"F0.wireOp",EDGE,"E0.bottom");Q2=makeQuery(id+"F11.boolean.opBoolean","SPLIT",EDGE,{"disambiguationData":[TD([makeQuery(id+"F11.opExtrude","SWEPT_FACE",FACE,{"disambiguationData":[OSD([sQuery(id+"F10.wireOp",EDGE,"E250")])]})])],"derivedFrom":makeQuery(id+"F3.opSweep","SWEPT_EDGE",EDGE,{"disambiguationData":[OSD([subQ2,subQ1,subQ0])]})});}
            var Q3;
            {var subQ0=sQuery(id+"F2.wireOp",EDGE,"E12");var subQ2=sQuery(id+"F0.wireOp",EDGE,"E0.top");var subQ3=sQuery(id+"F0.wireOp",EDGE,"E0.right");Q3=makeQuery(id+"F13.boolean.opBoolean","SPLIT",EDGE,{"disambiguationData":[TD([makeQuery(id+"F13.opExtrude","SWEPT_FACE",FACE,{"disambiguationData":[OSD([sQuery(id+"F12.wireOp",EDGE,"E267")])]})])],"derivedFrom":makeQuery(id+"F3.opSweep","SWEPT_EDGE",EDGE,{"disambiguationData":[OSD([subQ2,subQ3,subQ0])]})});}
            fillet(context, id + "F21", {"entities" : qUnion([Q0, Q1, Q2, Q3]), "radius" : 0.4 * mm, "tangentPropagation" : true, "allowEdgeOverflow" : false});
        }
    });
